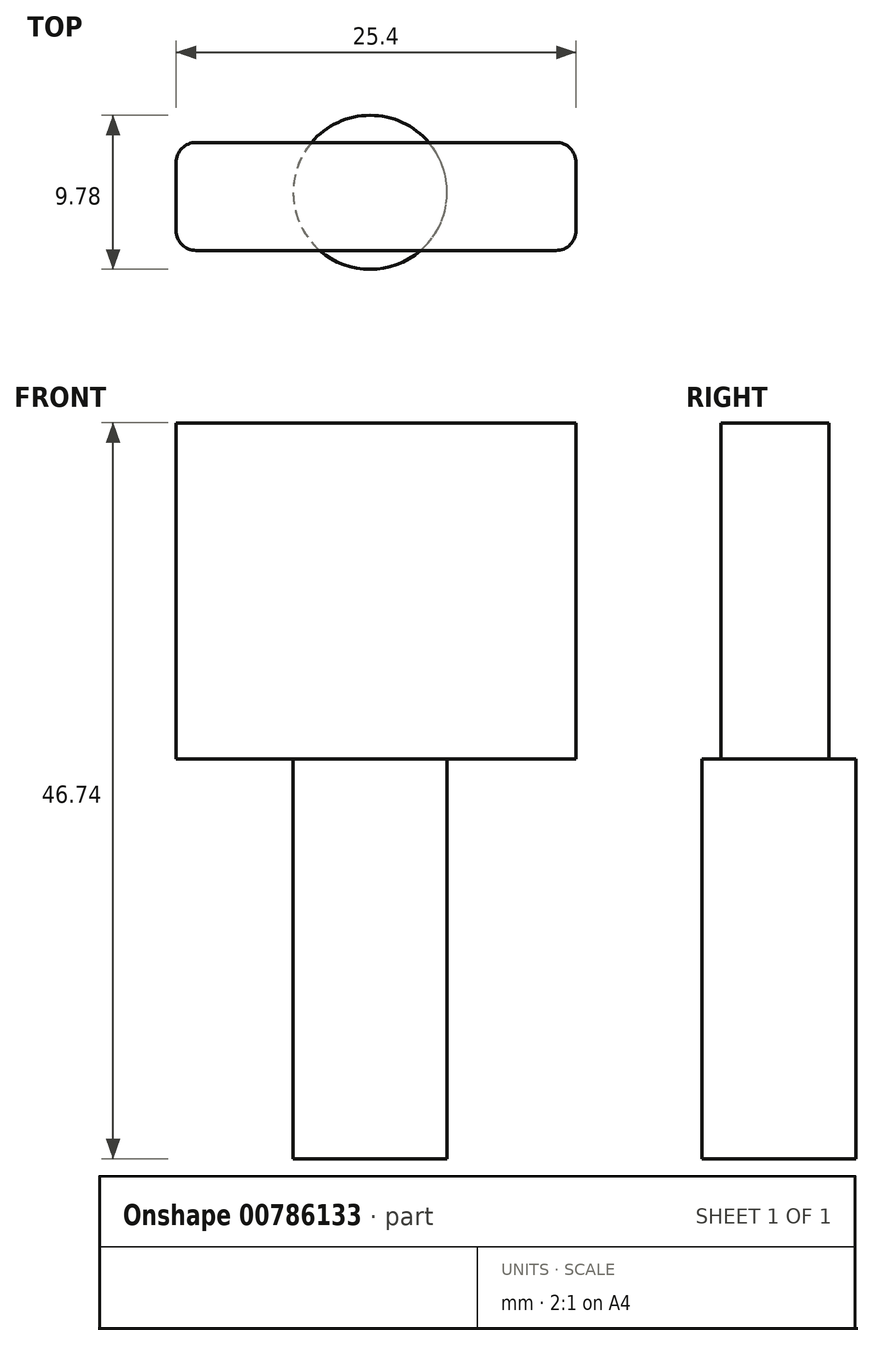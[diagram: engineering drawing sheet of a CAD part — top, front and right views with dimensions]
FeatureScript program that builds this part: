
annotation { "Feature Type Name" : "Feature", "Feature Type Description" : "" }
export const myFeature = defineFeature(function(context is Context, id is Id, definition is map)
    precondition{}
    {
        {
            var Q0;
            Q0=qCreatedBy(makeId("Top.planeOp"),FACE);
            var sketch = newSketch(context, id + "F0", { "sketchPlane" : qUnion([Q0])});
            skCircle(sketch, "E0", {"center": v(0, 0) * mm, "radius": 4.89 * mm});
            skSolve(sketch);
        }
        {
            var Q0;
            Q0=makeQuery(id+"F0.imprint","IMPRINT",FACE,{"disambiguationData":[TD([[makeQuery(id+"F0.imprint","IMPRINT",EDGE,{"derivedFrom":sQuery(id+"F0.wireOp",EDGE,"E0")}),1.0]])]});
            extrude(context, id + "F1", {"entities" : qUnion([Q0]), "depth" : 25.4 * mm, "offsetDistance" : 25.4 * mm});
        }
        {
            var Q0;
            Q0=makeQuery(id+"F1.opExtrude","CAP_FACE",FACE,{"disambiguationData":[OSD([sQuery(id+"F0.wireOp",EDGE,"E0")])],"isStart":false});
            var sketch = newSketch(context, id + "F2", { "sketchPlane" : qUnion([Q0])});
            skLineSegment(sketch, "E1.bottom", {"start": v(-11.05, 3.17) * mm, "end": v(11.8, 3.17) * mm});
            skLineSegment(sketch, "E1.top", {"start": v(-11.05, -3.7) * mm, "end": v(11.8, -3.7) * mm});
            skLineSegment(sketch, "E1.left", {"start": v(-12.32, 1.9) * mm, "end": v(-12.32, -2.42) * mm});
            skLineSegment(sketch, "E1.right", {"start": v(13.08, 1.9) * mm, "end": v(13.08, -2.42) * mm});
            skPoint(sketch, "E2.visualSharp", {"position": v(13.08, 3.17) * mm});
            skArc(sketch, "E2.filletArc", {"start": v(13.08, 1.9) * mm, "mid": v(12.7, 2.8) * mm, "end": v(11.8, 3.17) * mm});
            skPoint(sketch, "E3.visualSharp", {"position": v(13.08, -3.7) * mm});
            skArc(sketch, "E3.filletArc", {"start": v(11.8, -3.7) * mm, "mid": v(12.7, -3.32) * mm, "end": v(13.08, -2.42) * mm});
            skPoint(sketch, "E4.visualSharp", {"position": v(-12.32, -3.7) * mm});
            skArc(sketch, "E4.filletArc", {"start": v(-12.32, -2.42) * mm, "mid": v(-11.95, -3.32) * mm, "end": v(-11.05, -3.7) * mm});
            skPoint(sketch, "E5.visualSharp", {"position": v(-12.32, 3.17) * mm});
            skArc(sketch, "E5.filletArc", {"start": v(-11.05, 3.17) * mm, "mid": v(-11.95, 2.8) * mm, "end": v(-12.32, 1.9) * mm});
            skSolve(sketch);
        }
        {
            var Q0;
            Q0 = qSketchRegion(id + "F2", true);
            extrude(context, id + "F3", {"entities" : qUnion([Q0]), "operationType" : NewBodyOperationType.ADD, "depth" : 21.34 * mm, "offsetDistance" : 25.4 * mm});
        }
    });
